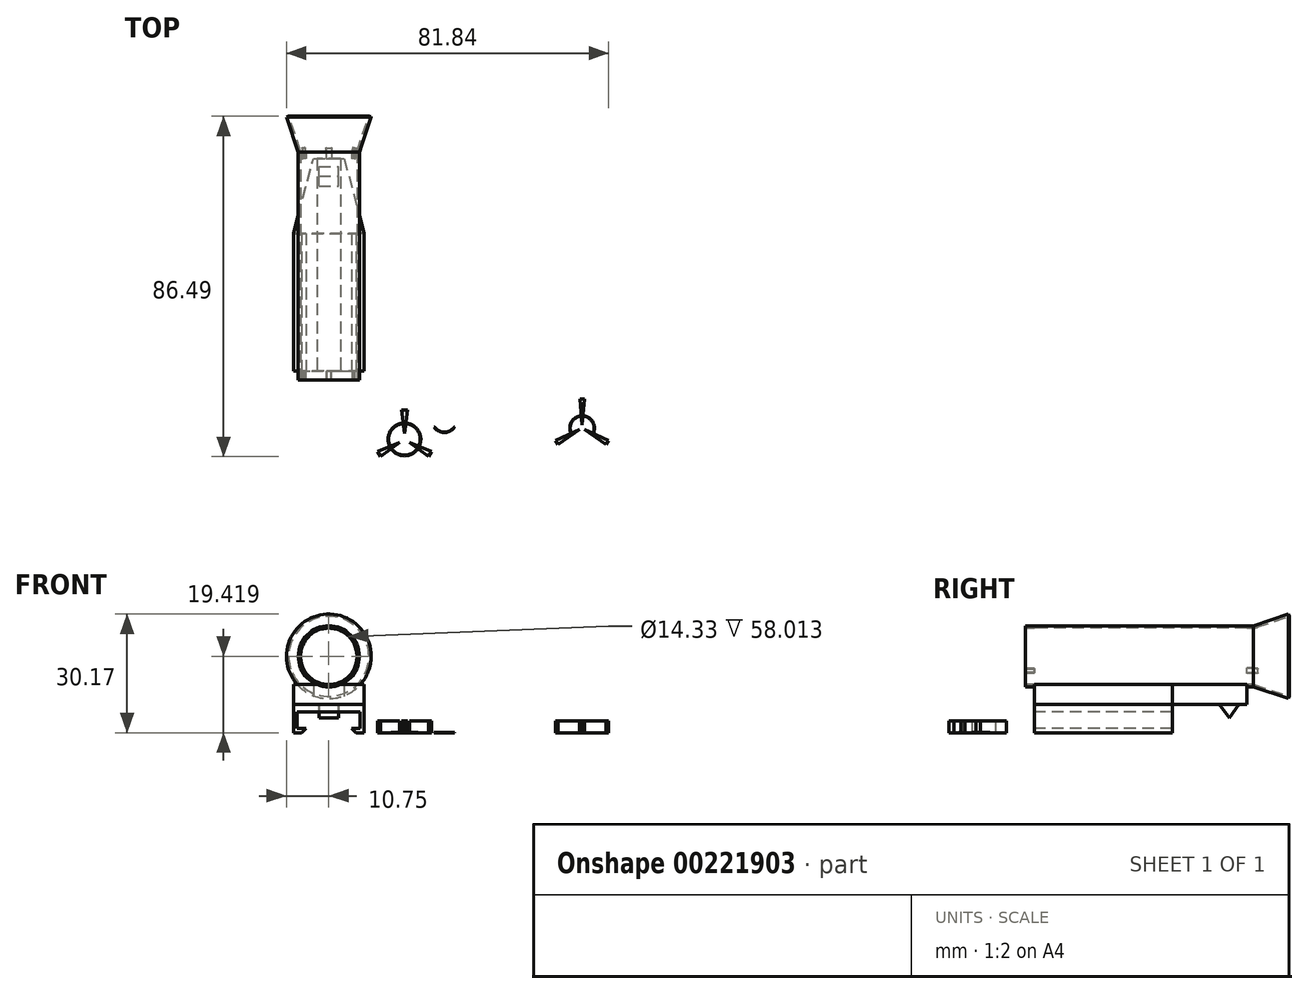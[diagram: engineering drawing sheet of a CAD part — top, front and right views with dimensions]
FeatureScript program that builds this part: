
annotation { "Feature Type Name" : "Feature", "Feature Type Description" : "" }
export const myFeature = defineFeature(function(context is Context, id is Id, definition is map)
    precondition{}
    {
        {
            var Q0;
            Q0=qCreatedBy(makeId("Top.planeOp"),FACE);
            var sketch = newSketch(context, id + "F0", { "sketchPlane" : qUnion([Q0])});
            skLineSegment(sketch, "E0.left", {"start": v(-9, 7.24) * mm, "end": v(-9, 0) * mm});
            skLineSegment(sketch, "E1", {"start": v(-9, 7.24) * mm, "end": v(0, 7.24) * mm});
            skLineSegment(sketch, "E2", {"start": v(-9, 0) * mm, "end": v(-6.97, 0) * mm});
            skLineSegment(sketch, "E3", {"start": v(-6.97, 0) * mm, "end": v(-5.83, 1.14) * mm});
            skLineSegment(sketch, "E4", {"start": v(-5.83, 1.14) * mm, "end": v(-8, 1.14) * mm});
            skLineSegment(sketch, "E5", {"start": v(-8, 1.14) * mm, "end": v(-8, 5.24) * mm});
            skLineSegment(sketch, "E6", {"start": v(-8, 5.24) * mm, "end": v(-0.18, 5.24) * mm});
            skLineSegment(sketch, "E7", {"start": v(-0.18, 5.24) * mm, "end": v(0, 5.24) * mm});
            skLineSegment(sketch, "E8.MirrorCS", {"start": v(9, 7.24) * mm, "end": v(0, 7.24) * mm});
            skLineSegment(sketch, "E9.MirrorCS", {"start": v(8, 5.24) * mm, "end": v(0.18, 5.24) * mm});
            skLineSegment(sketch, "E10.MirrorCS", {"start": v(9, 7.24) * mm, "end": v(9, 0) * mm});
            skLineSegment(sketch, "E11.MirrorCS", {"start": v(8, 1.14) * mm, "end": v(8, 5.24) * mm});
            skLineSegment(sketch, "E12.MirrorCS", {"start": v(5.83, 1.14) * mm, "end": v(8, 1.14) * mm});
            skLineSegment(sketch, "E13.MirrorCS", {"start": v(6.97, 0) * mm, "end": v(5.83, 1.14) * mm});
            skLineSegment(sketch, "E14.MirrorCS", {"start": v(9, 0) * mm, "end": v(6.97, 0) * mm});
            skLineSegment(sketch, "E15", {"start": v(0, 5.24) * mm, "end": v(0.18, 5.24) * mm});
            skSolve(sketch);
        }
        {
            var Q0;
            Q0=qSketchRegion(id+"F0",true);
            extrude(context, id + "F1", {"entities" : qUnion([Q0]), "depth" : 35 * mm});
        }
        {
            var Q0;
            Q0=qCreatedBy(makeId("Right.planeOp"),FACE);
            var sketch = newSketch(context, id + "F2", { "sketchPlane" : qUnion([Q0])});
            skLineSegment(sketch, "E16", {"start": v(7.24, 24.99) * mm, "end": v(7.24, 53.34) * mm, "construction": true});
            skLineSegment(sketch, "E17", {"start": v(7.24, 47) * mm, "end": v(3.74, 49.5) * mm});
            skLineSegment(sketch, "E18", {"start": v(3.74, 49.5) * mm, "end": v(7.24, 52) * mm});
            skLineSegment(sketch, "E19", {"start": v(7.24, 47) * mm, "end": v(7.24, 52) * mm});
            skSolve(sketch);
        }
        {
            var Q0;
            Q0=qSketchRegion(id+"F2",true);
            extrude(context, id + "F3", {"entities" : qUnion([Q0]), "depth" : 2.5 * mm, "hasSecondDirection" : true, "secondDirectionOppositeDirection" : true, "secondDirectionDepth" : 2.5 * mm});
        }
        {
            var Q0;
            Q0=makeQuery(id+"F3.opExtrude","SWEPT_BODY",BODY,{"disambiguationData":[OSD([sQuery(id+"F2.wireOp",EDGE,"E17"),sQuery(id+"F2.wireOp",EDGE,"E18"),sQuery(id+"F2.wireOp",EDGE,"E19")])]});
            var Q1;
            Q1=makeQuery(id+"F1.opExtrude","SWEPT_BODY",BODY,{"disambiguationData":[OSD([sQuery(id+"F0.wireOp",EDGE,"E0.left"),sQuery(id+"F0.wireOp",EDGE,"E1"),sQuery(id+"F0.wireOp",EDGE,"E2"),sQuery(id+"F0.wireOp",EDGE,"E3"),sQuery(id+"F0.wireOp",EDGE,"E4"),sQuery(id+"F0.wireOp",EDGE,"E5"),sQuery(id+"F0.wireOp",EDGE,"E6"),sQuery(id+"F0.wireOp",EDGE,"E7"),sQuery(id+"F0.wireOp",EDGE,"E8.MirrorCS"),sQuery(id+"F0.wireOp",EDGE,"E9.MirrorCS"),sQuery(id+"F0.wireOp",EDGE,"E10.MirrorCS"),sQuery(id+"F0.wireOp",EDGE,"E11.MirrorCS"),sQuery(id+"F0.wireOp",EDGE,"E12.MirrorCS"),sQuery(id+"F0.wireOp",EDGE,"E13.MirrorCS"),sQuery(id+"F0.wireOp",EDGE,"E14.MirrorCS"),sQuery(id+"F0.wireOp",EDGE,"E15")])]});
            var Q2;
            Q2=makeQuery(id+"F1.opExtrude","SWEPT_EDGE",EDGE,{"disambiguationData":[OSD([sQuery(id+"F0.wireOp",EDGE,"E0.left"),sQuery(id+"F0.wireOp",EDGE,"E1")])]});
            transform(context, id + "F4", {"entities" : qUnion([Q0, Q1]), "transformType" : TransformType.ROTATION, "transformAxis" : qUnion([Q2]), "angle" : 180 * degree, "makeCopy" : false});
        }
        {
            var Q0;
            Q0=makeQuery(id+"F1.opExtrude","SWEPT_BODY",BODY,{"disambiguationData":[OSD([sQuery(id+"F0.wireOp",EDGE,"E0.left"),sQuery(id+"F0.wireOp",EDGE,"E1"),sQuery(id+"F0.wireOp",EDGE,"E2"),sQuery(id+"F0.wireOp",EDGE,"E3"),sQuery(id+"F0.wireOp",EDGE,"E4"),sQuery(id+"F0.wireOp",EDGE,"E5"),sQuery(id+"F0.wireOp",EDGE,"E6"),sQuery(id+"F0.wireOp",EDGE,"E7"),sQuery(id+"F0.wireOp",EDGE,"E8.MirrorCS"),sQuery(id+"F0.wireOp",EDGE,"E9.MirrorCS"),sQuery(id+"F0.wireOp",EDGE,"E10.MirrorCS"),sQuery(id+"F0.wireOp",EDGE,"E11.MirrorCS"),sQuery(id+"F0.wireOp",EDGE,"E12.MirrorCS"),sQuery(id+"F0.wireOp",EDGE,"E13.MirrorCS"),sQuery(id+"F0.wireOp",EDGE,"E14.MirrorCS"),sQuery(id+"F0.wireOp",EDGE,"E15")])]});
            var Q1;
            Q1=makeQuery(id+"F3.opExtrude","SWEPT_BODY",BODY,{"disambiguationData":[OSD([sQuery(id+"F2.wireOp",EDGE,"E17"),sQuery(id+"F2.wireOp",EDGE,"E18"),sQuery(id+"F2.wireOp",EDGE,"E19")])]});
            var Q2;
            Q2=makeQuery(id+"F1.opExtrude","CAP_EDGE",EDGE,{"disambiguationData":[OSD([sQuery(id+"F0.wireOp",EDGE,"E14.MirrorCS")])],"isStart":true});
            transform(context, id + "F5", {"entities" : qUnion([Q0, Q1]), "transformType" : TransformType.ROTATION, "transformAxis" : qUnion([Q2]), "angle" : 90 * degree, "oppositeDirection" : true, "makeCopy" : false});
        }
        {
            var Q0;
            Q0=makeQuery(id+"F1.opExtrude","SWEPT_FACE",FACE,{"disambiguationData":[OSD([sQuery(id+"F0.wireOp",EDGE,"E1"),sQuery(id+"F0.wireOp",EDGE,"E8.MirrorCS")])]});
            var sketch = newSketch(context, id + "F6", { "sketchPlane" : qUnion([Q0])});
            skLineSegment(sketch, "E20.top", {"start": v(-27, 14.48) * mm, "end": v(-9, 14.48) * mm});
            skLineSegment(sketch, "E20.left", {"start": v(-27, 49.48) * mm, "end": v(-27, 14.48) * mm});
            skLineSegment(sketch, "E20.right", {"start": v(-9, 49.48) * mm, "end": v(-9, 14.48) * mm});
            skLineSegment(sketch, "E21", {"start": v(-27, 49.48) * mm, "end": v(-21.9, 68.48) * mm});
            skLineSegment(sketch, "E22", {"start": v(-21.9, 68.48) * mm, "end": v(-14.1, 68.48) * mm});
            skLineSegment(sketch, "E23", {"start": v(-14.1, 68.48) * mm, "end": v(-9, 49.48) * mm});
            skSolve(sketch);
        }
        {
            var Q0;
            Q0 = qSketchRegion(id + "F6", true);
            extrude(context, id + "F7", {"entities" : qUnion([Q0]), "depth" : 5 * mm});
        }
        {
            var Q0;
            Q0=makeQuery(id+"F7.opExtrude","SWEPT_FACE",FACE,{"disambiguationData":[OSD([sQuery(id+"F6.wireOp",EDGE,"E20.right")])]});
            cPlane(context, id + "F8", {"entities" : qUnion([Q0]), "cplaneType" : CPlaneType.OFFSET, "offset" : 9 * mm, "oppositeDirection" : true, "width" : 150 * mm, "height" : 150 * mm});
        }
        {
            var Q0;
            Q0=qCreatedBy(id+"F8.planeOp",FACE);
            var sketch = newSketch(context, id + "F9", { "sketchPlane" : qUnion([Q0])});
            skPoint(sketch, "E24.startSnap0", {"position": v(14.48, 9.74) * mm});
            skLineSegment(sketch, "E25.MirrorCS", {"start": v(79.25, 9.24) * mm, "end": v(79.06, 8.67) * mm});
            skLineSegment(sketch, "E26.MirrorCS", {"start": v(12.26, 12.26) * mm, "end": v(12.26, 11.66) * mm});
            skLineSegment(sketch, "E27.MirrorCS", {"start": v(70.27, 19.42) * mm, "end": v(79.25, 19.42) * mm});
            skLineSegment(sketch, "E28.MirrorCS", {"start": v(12.26, 12.26) * mm, "end": v(70.27, 12.26) * mm});
            skLineSegment(sketch, "E29.MirrorCS", {"start": v(70.27, 12.26) * mm, "end": v(79.25, 9.24) * mm});
            skLineSegment(sketch, "E30.MirrorCS", {"start": v(70.18, 11.66) * mm, "end": v(79.06, 8.67) * mm});
            skLineSegment(sketch, "E31.MirrorCS", {"start": v(12.26, 11.66) * mm, "end": v(70.18, 11.66) * mm});
            skLineSegment(sketch, "E32.MirrorCS", {"start": v(12.26, 19.42) * mm, "end": v(82.66, 19.42) * mm, "construction": true});
            skLineSegment(sketch, "E33.MirrorCS", {"start": v(79.25, 9.24) * mm, "end": v(79.25, 19.42) * mm});
            skLineSegment(sketch, "E34.MirrorCS", {"start": v(70.27, 12.26) * mm, "end": v(70.27, 19.42) * mm});
            skSolve(sketch);
        }
        {
            var Q0;
            Q0=makeQuery(id+"F9.imprint","IMPRINT",FACE,{"disambiguationData":[TD([[makeQuery(id+"F9.imprint","IMPRINT",EDGE,{"derivedFrom":sQuery(id+"F9.wireOp",EDGE,"E25.MirrorCS")}),-1.0]])]});
            var Q1;
            Q1=sQuery(id+"F9.wireOp",EDGE,"E32.MirrorCS");
            revolve(context, id + "F10", {"operationType" : NewBodyOperationType.ADD, "entities" : qUnion([Q0]), "axis" : qUnion([Q1]), "revolveType" : RevolveType.FULL});
        }
        {
            var Q0;
            Q0=makeQuery(id+"F7.opExtrude","SWEPT_FACE",FACE,{"disambiguationData":[OSD([sQuery(id+"F6.wireOp",EDGE,"E22")])]});
            var sketch = newSketch(context, id + "F11", { "sketchPlane" : qUnion([Q0])});
            skLineSegment(sketch, "E35", {"start": v(17.25, 26.87) * mm, "end": v(18, 20.92) * mm});
            skLineSegment(sketch, "E36", {"start": v(18, 20.92) * mm, "end": v(18.75, 26.87) * mm});
            skLineSegment(sketch, "E37", {"start": v(18.75, 26.87) * mm, "end": v(17.25, 26.87) * mm});
            skLineSegment(sketch, "E38", {"start": v(18, 20.92) * mm, "end": v(18, 19.42) * mm, "construction": true});
            skLineSegment(sketch, "E39.1.0", {"start": v(11.92, 15.04) * mm, "end": v(16.7, 18.67) * mm});
            skLineSegment(sketch, "E39.1.1", {"start": v(16.7, 18.67) * mm, "end": v(11.17, 16.34) * mm});
            skLineSegment(sketch, "E39.1.2", {"start": v(11.17, 16.34) * mm, "end": v(11.92, 15.04) * mm});
            skLineSegment(sketch, "E39.2.0", {"start": v(24.83, 16.34) * mm, "end": v(19.3, 18.67) * mm});
            skLineSegment(sketch, "E39.2.1", {"start": v(19.3, 18.67) * mm, "end": v(24.08, 15.04) * mm});
            skLineSegment(sketch, "E39.2.2", {"start": v(24.08, 15.04) * mm, "end": v(24.83, 16.34) * mm});
            skPoint(sketch, "E39.center", {"position": v(18, 19.42) * mm});
            skLineSegment(sketch, "E40", {"start": v(19.3, 18.67) * mm, "end": v(18, 19.42) * mm, "construction": true});
            skLineSegment(sketch, "E41", {"start": v(16.7, 18.67) * mm, "end": v(18, 19.42) * mm, "construction": true});
            skSolve(sketch);
        }
        {
            var Q0;
            Q0=makeQuery(id+"F11.imprint","IMPRINT",FACE,{"disambiguationData":[TD([[makeQuery(id+"F11.imprint","IMPRINT",EDGE,{"derivedFrom":sQuery(id+"F11.wireOp",EDGE,"E39.1.0")}),1.0]])]});
            var Q1;
            Q1=makeQuery(id+"F11.imprint","IMPRINT",FACE,{"disambiguationData":[TD([[makeQuery(id+"F11.imprint","IMPRINT",EDGE,{"derivedFrom":sQuery(id+"F11.wireOp",EDGE,"E39.2.0")}),1.0]])]});
            var Q2;
            Q2=makeQuery(id+"F11.imprint","IMPRINT",FACE,{"disambiguationData":[TD([[makeQuery(id+"F11.imprint","IMPRINT",EDGE,{"derivedFrom":sQuery(id+"F11.wireOp",EDGE,"E35")}),1.0]])]});
            extrude(context, id + "F12", {"entities" : qUnion([Q0, Q1, Q2]), "operationType" : NewBodyOperationType.REMOVE, "depth" : 25 * mm});
        }
        {
            var Q0;
            Q0=makeQuery(id+"F7.opExtrude","SWEPT_FACE",FACE,{"disambiguationData":[OSD([sQuery(id+"F6.wireOp",EDGE,"E20.top")])]});
            var sketch = newSketch(context, id + "F13", { "sketchPlane" : qUnion([Q0])});
            skLineSegment(sketch, "E42", {"start": v(-18.6, 26.84) * mm, "end": v(-17.4, 26.84) * mm});
            skLineSegment(sketch, "E43", {"start": v(-17.4, 26.84) * mm, "end": v(-18, 20.17) * mm});
            skLineSegment(sketch, "E44", {"start": v(-18, 20.17) * mm, "end": v(-18.6, 26.84) * mm});
            skLineSegment(sketch, "E45", {"start": v(-18, 20.17) * mm, "end": v(-18, 19.42) * mm, "construction": true});
            skLineSegment(sketch, "E46.1.0", {"start": v(-24.73, 16.23) * mm, "end": v(-18.65, 19.04) * mm});
            skLineSegment(sketch, "E46.1.1", {"start": v(-18.65, 19.04) * mm, "end": v(-24.13, 15.19) * mm});
            skLineSegment(sketch, "E46.1.2", {"start": v(-24.13, 15.19) * mm, "end": v(-24.73, 16.23) * mm});
            skLineSegment(sketch, "E46.2.0", {"start": v(-11.87, 15.19) * mm, "end": v(-17.35, 19.04) * mm});
            skLineSegment(sketch, "E46.2.1", {"start": v(-17.35, 19.04) * mm, "end": v(-11.27, 16.23) * mm});
            skLineSegment(sketch, "E46.2.2", {"start": v(-11.27, 16.23) * mm, "end": v(-11.87, 15.19) * mm});
            skPoint(sketch, "E46.center", {"position": v(-18, 19.42) * mm});
            skSolve(sketch);
        }
        {
            var Q0;
            Q0 = qSketchRegion(id + "F13", true);
            extrude(context, id + "F14", {"entities" : qUnion([Q0]), "operationType" : NewBodyOperationType.REMOVE, "endBound" : BoundingType.THROUGH_ALL, "depth" : 25 * mm});
        }
        {
            var Q0;
            Q0=qCreatedBy(makeId("Top.planeOp"),FACE);
            var sketch = newSketch(context, id + "F15", { "sketchPlane" : qUnion([Q0])});
            skCircle(sketch, "E47", {"center": v(46.36, 0) * mm, "radius": 7.45 * mm, "construction": true});
            skLineSegment(sketch, "E48", {"start": v(46.96, 7.42) * mm, "end": v(46.36, 0.75) * mm});
            skLineSegment(sketch, "E49", {"start": v(46.36, 0.75) * mm, "end": v(45.76, 7.42) * mm});
            skLineSegment(sketch, "E50", {"start": v(45.76, 7.42) * mm, "end": v(46.96, 7.42) * mm});
            skLineSegment(sketch, "E51.1.0", {"start": v(39.63, -3.2) * mm, "end": v(45.7, -0.37) * mm});
            skLineSegment(sketch, "E51.1.1", {"start": v(45.7, -0.37) * mm, "end": v(40.23, -4.23) * mm});
            skLineSegment(sketch, "E51.1.2", {"start": v(40.23, -4.23) * mm, "end": v(39.63, -3.2) * mm});
            skLineSegment(sketch, "E51.2.0", {"start": v(52.49, -4.23) * mm, "end": v(47, -0.37) * mm});
            skLineSegment(sketch, "E51.2.1", {"start": v(47, -0.37) * mm, "end": v(53.09, -3.2) * mm});
            skLineSegment(sketch, "E51.2.2", {"start": v(53.09, -3.2) * mm, "end": v(52.49, -4.23) * mm});
            skCircle(sketch, "E52", {"center": v(1.22, -2.87) * mm, "radius": 7.5 * mm, "construction": true});
            skLineSegment(sketch, "E53", {"start": v(1.97, 4.59) * mm, "end": v(1.22, -1.37) * mm});
            skLineSegment(sketch, "E54", {"start": v(1.22, -1.37) * mm, "end": v(0.47, 4.59) * mm});
            skLineSegment(sketch, "E55", {"start": v(0.47, 4.59) * mm, "end": v(1.97, 4.59) * mm});
            skLineSegment(sketch, "E56.1.0", {"start": v(-5.6, -5.94) * mm, "end": v(-0.08, -3.62) * mm});
            skLineSegment(sketch, "E56.1.1", {"start": v(-0.08, -3.62) * mm, "end": v(-4.86, -7.24) * mm});
            skLineSegment(sketch, "E56.1.2", {"start": v(-4.86, -7.24) * mm, "end": v(-5.6, -5.94) * mm});
            skLineSegment(sketch, "E56.2.0", {"start": v(7.3, -7.24) * mm, "end": v(2.52, -3.62) * mm});
            skLineSegment(sketch, "E56.2.1", {"start": v(2.52, -3.62) * mm, "end": v(8.05, -5.94) * mm});
            skLineSegment(sketch, "E56.2.2", {"start": v(8.05, -5.94) * mm, "end": v(7.3, -7.24) * mm});
            skCircle(sketch, "E57", {"center": v(1.22, -2.87) * mm, "radius": 4.02 * mm});
            skCircle(sketch, "E58", {"center": v(1.22, -2.87) * mm, "radius": 4.16 * mm});
            skCircle(sketch, "E59", {"center": v(46.36, 0) * mm, "radius": 3.04 * mm});
            skCircle(sketch, "E60", {"center": v(46.36, 0) * mm, "radius": 3.14 * mm});
            skSolve(sketch);
        }
        {
            var Q0;
            Q0=makeQuery(id+"F15.imprint","IMPRINT",FACE,{"disambiguationData":[TD([[makeQuery(id+"F15.imprint","IMPRINT",EDGE,{"derivedFrom":sQuery(id+"F15.wireOp",EDGE,"E56.2.0")}),-1.0]])]});
            var Q1;
            Q1=makeQuery(id+"F15.imprint","IMPRINT",FACE,{"disambiguationData":[TD([[makeQuery(id+"F15.imprint","IMPRINT",EDGE,{"derivedFrom":sQuery(id+"F15.wireOp",EDGE,"E53")}),-1.0]])]});
            var Q2;
            Q2=makeQuery(id+"F15.imprint","IMPRINT",FACE,{"disambiguationData":[TD([[makeQuery(id+"F15.imprint","IMPRINT",EDGE,{"derivedFrom":sQuery(id+"F15.wireOp",EDGE,"E56.1.0")}),-1.0]])]});
            var Q3;
            Q3=makeQuery(id+"F15.imprint","IMPRINT",FACE,{"disambiguationData":[TD([[makeQuery(id+"F15.imprint","IMPRINT",EDGE,{"derivedFrom":sQuery(id+"F15.wireOp",EDGE,"E51.1.0")}),-1.0]])]});
            var Q4;
            Q4=makeQuery(id+"F15.imprint","IMPRINT",FACE,{"disambiguationData":[TD([[makeQuery(id+"F15.imprint","IMPRINT",EDGE,{"derivedFrom":sQuery(id+"F15.wireOp",EDGE,"E51.2.0")}),-1.0]])]});
            var Q5;
            Q5=makeQuery(id+"F15.imprint","IMPRINT",FACE,{"disambiguationData":[TD([[makeQuery(id+"F15.imprint","IMPRINT",EDGE,{"derivedFrom":sQuery(id+"F15.wireOp",EDGE,"E48")}),-1.0]])]});
            var Q6;
            {var subQ0=sQuery(id+"F15.wireOp",EDGE,"E56.2.2");Q6=makeQuery(id+"F15.imprint","IMPRINT",FACE,{"disambiguationData":[TD([[makeQuery(id+"F15.imprint","IMPRINT",EDGE,{"derivedFrom":subQ0}),-1.0]])]});}
            var Q7;
            {var subQ0=sQuery(id+"F15.wireOp",EDGE,"E55");Q7=makeQuery(id+"F15.imprint","IMPRINT",FACE,{"disambiguationData":[TD([[makeQuery(id+"F15.imprint","IMPRINT",EDGE,{"derivedFrom":subQ0}),-1.0]])]});}
            var Q8;
            {var subQ0=sQuery(id+"F15.wireOp",EDGE,"E56.1.2");Q8=makeQuery(id+"F15.imprint","IMPRINT",FACE,{"disambiguationData":[TD([[makeQuery(id+"F15.imprint","IMPRINT",EDGE,{"derivedFrom":subQ0}),-1.0]])]});}
            var Q9;
            {var subQ0=sQuery(id+"F15.wireOp",EDGE,"E58");var subQ1=sQuery(id+"F15.wireOp",EDGE,"E56.1.0");var subQ2=makeQuery(id+"F15.imprint","INTERSECT",VERTEX,{"derivedFrom":[subQ1,subQ0]});Q9=makeQuery(id+"F15.imprint","IMPRINT",FACE,{"disambiguationData":[TD([[makeQuery(id+"F15.imprint","IMPRINT",EDGE,{"disambiguationData":[TD([[subQ2,-1.0]])],"derivedFrom":subQ1}),-1.0]])]});}
            var Q10;
            {var subQ0=sQuery(id+"F15.wireOp",EDGE,"E58");var subQ1=sQuery(id+"F15.wireOp",EDGE,"E53");var subQ2=makeQuery(id+"F15.imprint","INTERSECT",VERTEX,{"derivedFrom":[subQ1,subQ0]});Q10=makeQuery(id+"F15.imprint","IMPRINT",FACE,{"disambiguationData":[TD([[makeQuery(id+"F15.imprint","IMPRINT",EDGE,{"disambiguationData":[TD([[subQ2,-1.0]])],"derivedFrom":subQ1}),-1.0]])]});}
            var Q11;
            {var subQ0=sQuery(id+"F15.wireOp",EDGE,"E58");var subQ1=sQuery(id+"F15.wireOp",EDGE,"E56.2.0");var subQ2=makeQuery(id+"F15.imprint","INTERSECT",VERTEX,{"derivedFrom":[subQ1,subQ0]});Q11=makeQuery(id+"F15.imprint","IMPRINT",FACE,{"disambiguationData":[TD([[makeQuery(id+"F15.imprint","IMPRINT",EDGE,{"disambiguationData":[TD([[subQ2,-1.0]])],"derivedFrom":subQ1}),-1.0]])]});}
            var Q12;
            {var subQ0=sQuery(id+"F15.wireOp",EDGE,"E60");var subQ1=sQuery(id+"F15.wireOp",EDGE,"E51.1.0");var subQ2=makeQuery(id+"F15.imprint","INTERSECT",VERTEX,{"derivedFrom":[subQ1,subQ0]});Q12=makeQuery(id+"F15.imprint","IMPRINT",FACE,{"disambiguationData":[TD([[makeQuery(id+"F15.imprint","IMPRINT",EDGE,{"disambiguationData":[TD([[subQ2,-1.0]])],"derivedFrom":subQ1}),-1.0]])]});}
            var Q13;
            {var subQ0=sQuery(id+"F15.wireOp",EDGE,"E51.1.2");Q13=makeQuery(id+"F15.imprint","IMPRINT",FACE,{"disambiguationData":[TD([[makeQuery(id+"F15.imprint","IMPRINT",EDGE,{"derivedFrom":subQ0}),-1.0]])]});}
            var Q14;
            {var subQ0=sQuery(id+"F15.wireOp",EDGE,"E60");var subQ1=sQuery(id+"F15.wireOp",EDGE,"E51.2.0");var subQ2=makeQuery(id+"F15.imprint","INTERSECT",VERTEX,{"derivedFrom":[subQ1,subQ0]});Q14=makeQuery(id+"F15.imprint","IMPRINT",FACE,{"disambiguationData":[TD([[makeQuery(id+"F15.imprint","IMPRINT",EDGE,{"disambiguationData":[TD([[subQ2,-1.0]])],"derivedFrom":subQ1}),-1.0]])]});}
            var Q15;
            {var subQ0=sQuery(id+"F15.wireOp",EDGE,"E51.2.2");Q15=makeQuery(id+"F15.imprint","IMPRINT",FACE,{"disambiguationData":[TD([[makeQuery(id+"F15.imprint","IMPRINT",EDGE,{"derivedFrom":subQ0}),-1.0]])]});}
            var Q16;
            {var subQ0=sQuery(id+"F15.wireOp",EDGE,"E60");var subQ1=sQuery(id+"F15.wireOp",EDGE,"E48");var subQ2=makeQuery(id+"F15.imprint","INTERSECT",VERTEX,{"derivedFrom":[subQ1,subQ0]});Q16=makeQuery(id+"F15.imprint","IMPRINT",FACE,{"disambiguationData":[TD([[makeQuery(id+"F15.imprint","IMPRINT",EDGE,{"disambiguationData":[TD([[subQ2,-1.0]])],"derivedFrom":subQ1}),-1.0]])]});}
            var Q17;
            {var subQ0=sQuery(id+"F15.wireOp",EDGE,"E50");Q17=makeQuery(id+"F15.imprint","IMPRINT",FACE,{"disambiguationData":[TD([[makeQuery(id+"F15.imprint","IMPRINT",EDGE,{"derivedFrom":subQ0}),-1.0]])]});}
            extrude(context, id + "F16", {"entities" : qUnion([Q0, Q1, Q2, Q3, Q4, Q5, Q6, Q7, Q8, Q9, Q10, Q11, Q12, Q13, Q14, Q15, Q16, Q17]), "depth" : 3 * mm});
        }
        {
            var Q0;
            {var subQ0=sQuery(id+"F15.wireOp",EDGE,"E58");var subQ1=sQuery(id+"F15.wireOp",EDGE,"E53");var subQ2=makeQuery(id+"F15.imprint","INTERSECT",VERTEX,{"derivedFrom":[subQ1,subQ0]});Q0=makeQuery(id+"F15.imprint","IMPRINT",FACE,{"disambiguationData":[TD([[makeQuery(id+"F15.imprint","IMPRINT",EDGE,{"disambiguationData":[TD([[subQ2,-1.0]])],"derivedFrom":subQ1}),1.0]])]});}
            var Q1;
            {var subQ0=sQuery(id+"F15.wireOp",EDGE,"E58");var subQ1=sQuery(id+"F15.wireOp",EDGE,"E56.1.1");var subQ2=makeQuery(id+"F15.imprint","INTERSECT",VERTEX,{"derivedFrom":[subQ1,subQ0]});Q1=makeQuery(id+"F15.imprint","IMPRINT",FACE,{"disambiguationData":[TD([[makeQuery(id+"F15.imprint","IMPRINT",EDGE,{"disambiguationData":[TD([[subQ2,1.0]])],"derivedFrom":subQ1}),1.0]])]});}
            var Q2;
            {var subQ0=sQuery(id+"F15.wireOp",EDGE,"E58");var subQ1=sQuery(id+"F15.wireOp",EDGE,"E54");var subQ2=makeQuery(id+"F15.imprint","INTERSECT",VERTEX,{"derivedFrom":[subQ1,subQ0]});Q2=makeQuery(id+"F15.imprint","IMPRINT",FACE,{"disambiguationData":[TD([[makeQuery(id+"F15.imprint","IMPRINT",EDGE,{"disambiguationData":[TD([[subQ2,1.0]])],"derivedFrom":subQ1}),1.0]])]});}
            var Q3;
            {var subQ0=sQuery(id+"F15.wireOp",EDGE,"E60");var subQ1=sQuery(id+"F15.wireOp",EDGE,"E49");var subQ2=makeQuery(id+"F15.imprint","INTERSECT",VERTEX,{"derivedFrom":[subQ1,subQ0]});Q3=makeQuery(id+"F15.imprint","IMPRINT",FACE,{"disambiguationData":[TD([[makeQuery(id+"F15.imprint","IMPRINT",EDGE,{"disambiguationData":[TD([[subQ2,1.0]])],"derivedFrom":subQ1}),1.0]])]});}
            var Q4;
            {var subQ0=sQuery(id+"F15.wireOp",EDGE,"E60");var subQ1=sQuery(id+"F15.wireOp",EDGE,"E48");var subQ2=makeQuery(id+"F15.imprint","INTERSECT",VERTEX,{"derivedFrom":[subQ1,subQ0]});Q4=makeQuery(id+"F15.imprint","IMPRINT",FACE,{"disambiguationData":[TD([[makeQuery(id+"F15.imprint","IMPRINT",EDGE,{"disambiguationData":[TD([[subQ2,-1.0]])],"derivedFrom":subQ1}),1.0]])]});}
            var Q5;
            {var subQ0=sQuery(id+"F15.wireOp",EDGE,"E60");var subQ1=sQuery(id+"F15.wireOp",EDGE,"E51.1.1");var subQ2=makeQuery(id+"F15.imprint","INTERSECT",VERTEX,{"derivedFrom":[subQ1,subQ0]});Q5=makeQuery(id+"F15.imprint","IMPRINT",FACE,{"disambiguationData":[TD([[makeQuery(id+"F15.imprint","IMPRINT",EDGE,{"disambiguationData":[TD([[subQ2,1.0]])],"derivedFrom":subQ1}),1.0]])]});}
            extrude(context, id + "F17", {"entities" : qUnion([Q0, Q1, Q2, Q3, Q4, Q5]), "depth" : 0.1 * mm});
        }
        {
            var Q0;
            Q0=makeQuery(id+"F17.opExtrude","SWEPT_BODY",BODY,{"disambiguationData":[OSD([sQuery(id+"F15.wireOp",EDGE,"E51.1.1"),sQuery(id+"F15.wireOp",EDGE,"E51.2.0"),sQuery(id+"F15.wireOp",EDGE,"E59"),sQuery(id+"F15.wireOp",EDGE,"E60")])]});
            transform(context, id + "F18", {"entities" : qUnion([Q0]), "transformType" : TransformType.TRANSLATION_3D, "dx" : -35 * mm, "dy" : 2 * mm, "dz" : 0 * mm, "makeCopy" : false});
        }
    });
